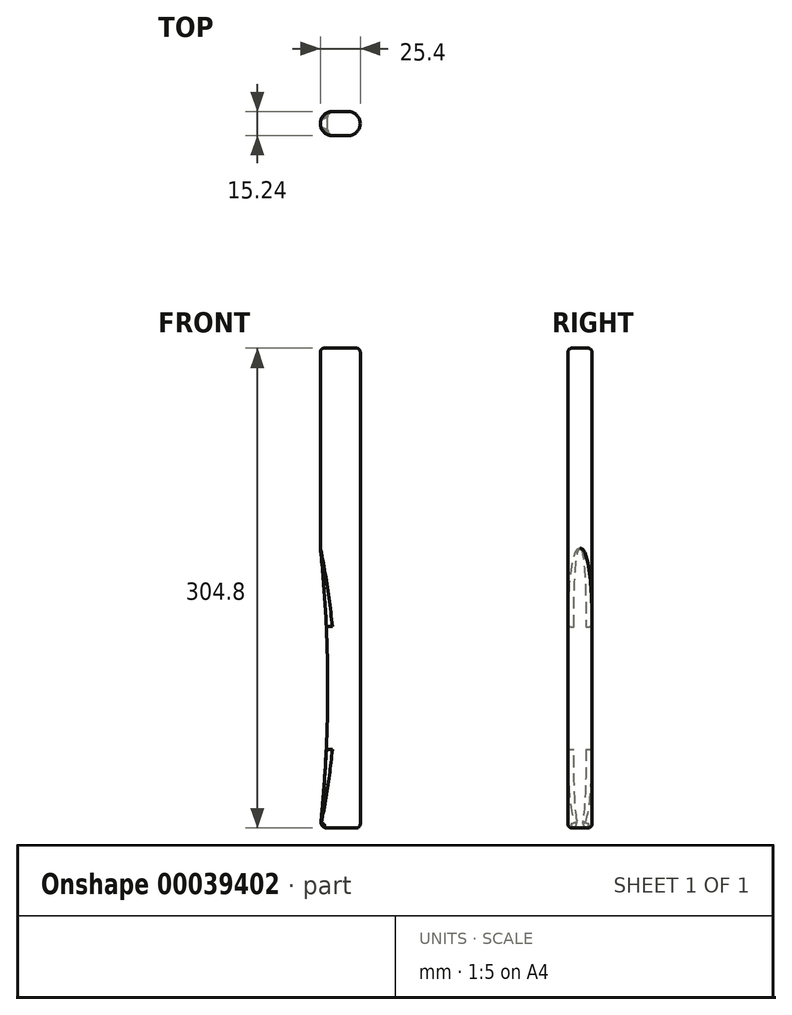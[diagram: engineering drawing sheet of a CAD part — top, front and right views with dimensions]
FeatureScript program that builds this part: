
annotation { "Feature Type Name" : "Feature", "Feature Type Description" : "" }
export const myFeature = defineFeature(function(context is Context, id is Id, definition is map)
    precondition{}
    {
        {
            var Q0;
            Q0=qCreatedBy(makeId("Front.planeOp"),FACE);
            var sketch = newSketch(context, id + "F0", { "sketchPlane" : qUnion([Q0])});
            skLineSegment(sketch, "E0", {"start": v(1.98, -144.5) * mm, "end": v(1.98, 160.3) * mm});
            skLineSegment(sketch, "E1", {"start": v(1.98, 160.3) * mm, "end": v(-23.42, 160.3) * mm});
            skLineSegment(sketch, "E2", {"start": v(-23.42, 160.3) * mm, "end": v(-23.42, 33.3) * mm});
            skLineSegment(sketch, "E3", {"start": v(1.98, -144.5) * mm, "end": v(-23.42, -144.5) * mm});
            skArc(sketch, "E4", {"start": v(-23.42, -144.5) * mm, "mid": v(-18.7, -55.6) * mm, "end": v(-23.42, 33.3) * mm});
            skSolve(sketch);
        }
        {
            var Q0;
            Q0 = qSketchRegion(id + "F0", true);
            extrude(context, id + "F1", {"entities" : qUnion([Q0]), "depth" : 15.24 * mm});
        }
        {
            var Q0;
            Q0=makeQuery(id+"F1.opExtrude","CAP_EDGE",EDGE,{"disambiguationData":[OSD([sQuery(id+"F0.wireOp",EDGE,"E0")])],"isStart":false});
            var Q1;
            Q1=makeQuery(id+"F1.opExtrude","CAP_EDGE",EDGE,{"disambiguationData":[OSD([sQuery(id+"F0.wireOp",EDGE,"E0")])],"isStart":true});
            var Q2;
            Q2=makeQuery(id+"F1.opExtrude","CAP_EDGE",EDGE,{"disambiguationData":[OSD([sQuery(id+"F0.wireOp",EDGE,"E2")])],"isStart":true});
            var Q3;
            Q3=makeQuery(id+"F1.opExtrude","CAP_EDGE",EDGE,{"disambiguationData":[OSD([sQuery(id+"F0.wireOp",EDGE,"E2")])],"isStart":false});
            var Q4;
            Q4=makeQuery(id+"F1.opExtrude","CAP_EDGE",EDGE,{"disambiguationData":[OSD([sQuery(id+"F0.wireOp",EDGE,"ed93cf97-2ccb-4e51-b4c0-a1d36dc98316")])],"isStart":true});
            var Q5;
            Q5=makeQuery(id+"F1.opExtrude","CAP_EDGE",EDGE,{"disambiguationData":[OSD([sQuery(id+"F0.wireOp",EDGE,"ed93cf97-2ccb-4e51-b4c0-a1d36dc98316")])],"isStart":false});
            fillet(context, id + "F2", {"entities" : qUnion([Q0, Q1, Q2, Q3, Q4, Q5]), "radius" : 7.62 * mm, "tangentPropagation" : true, "allowEdgeOverflow" : false});
        }
        {
            var Q0;
            Q0=makeQuery(id+"F1.opExtrude","CAP_EDGE",EDGE,{"disambiguationData":[OSD([sQuery(id+"F0.wireOp",EDGE,"E1")])],"isStart":false});
            var Q1;
            Q1=makeQuery(id+"F1.opExtrude","CAP_EDGE",EDGE,{"disambiguationData":[OSD([sQuery(id+"F0.wireOp",EDGE,"E1")])],"isStart":true});
            var Q2;
            Q2=makeQuery(id+"F2.opFillet","BLEND_EDGE",EDGE,{"blendedFrom":[makeQuery(id+"F1.opExtrude","CAP_EDGE",EDGE,{"disambiguationData":[OSD([sQuery(id+"F0.wireOp",EDGE,"E0")])],"isStart":false}),makeQuery(id+"F1.opExtrude","SWEPT_FACE",FACE,{"disambiguationData":[OSD([sQuery(id+"F0.wireOp",EDGE,"E1")])]})],"blendedInto":[makeQuery(id+"F1.opExtrude","SWEPT_FACE",FACE,{"disambiguationData":[OSD([sQuery(id+"F0.wireOp",EDGE,"E1")])]})]});
            var Q3;
            Q3=makeQuery(id+"F2.opFillet","BLEND_EDGE",EDGE,{"blendedFrom":[makeQuery(id+"F1.opExtrude","CAP_EDGE",EDGE,{"disambiguationData":[OSD([sQuery(id+"F0.wireOp",EDGE,"E2")])],"isStart":false}),makeQuery(id+"F1.opExtrude","SWEPT_FACE",FACE,{"disambiguationData":[OSD([sQuery(id+"F0.wireOp",EDGE,"E1")])]})],"blendedInto":[makeQuery(id+"F1.opExtrude","SWEPT_FACE",FACE,{"disambiguationData":[OSD([sQuery(id+"F0.wireOp",EDGE,"E1")])]})]});
            var Q4;
            Q4=makeQuery(id+"F2.opFillet","BLEND_EDGE",EDGE,{"blendedFrom":[makeQuery(id+"F1.opExtrude","CAP_EDGE",EDGE,{"disambiguationData":[OSD([sQuery(id+"F0.wireOp",EDGE,"E2")])],"isStart":false}),makeQuery(id+"F1.opExtrude","SWEPT_FACE",FACE,{"disambiguationData":[OSD([sQuery(id+"F0.wireOp",EDGE,"E3")])]})],"blendedInto":[makeQuery(id+"F1.opExtrude","SWEPT_FACE",FACE,{"disambiguationData":[OSD([sQuery(id+"F0.wireOp",EDGE,"E3")])]})]});
            fillet(context, id + "F3", {"entities" : qUnion([Q0, Q1, Q2, Q3, Q4]), "radius" : 2.54 * mm, "tangentPropagation" : true, "allowEdgeOverflow" : false});
        }
        {
            var Q0;
            Q0=makeQuery(id+"F2.opFillet","BLEND_EDGE",EDGE,{"blendedFrom":[makeQuery(id+"F1.opExtrude","CAP_EDGE",EDGE,{"disambiguationData":[OSD([sQuery(id+"F0.wireOp",EDGE,"E2")])],"isStart":false}),makeQuery(id+"F1.opExtrude","SWEPT_FACE",FACE,{"disambiguationData":[OSD([sQuery(id+"F0.wireOp",EDGE,"E4")])]})],"blendedInto":[makeQuery(id+"F1.opExtrude","SWEPT_FACE",FACE,{"disambiguationData":[OSD([sQuery(id+"F0.wireOp",EDGE,"E4")])]})]});
            var Q1;
            Q1=makeQuery(id+"F2.opFillet","BLEND_EDGE",EDGE,{"blendedFrom":[makeQuery(id+"F1.opExtrude","CAP_EDGE",EDGE,{"disambiguationData":[OSD([sQuery(id+"F0.wireOp",EDGE,"E2")])],"isStart":true}),makeQuery(id+"F1.opExtrude","SWEPT_FACE",FACE,{"disambiguationData":[OSD([sQuery(id+"F0.wireOp",EDGE,"E4")])]})],"blendedInto":[makeQuery(id+"F1.opExtrude","SWEPT_FACE",FACE,{"disambiguationData":[OSD([sQuery(id+"F0.wireOp",EDGE,"E4")])]})]});
            fillet(context, id + "F4", {"entities" : qUnion([Q0, Q1]), "radius" : 3.8 * mm, "tangentPropagation" : true, "allowEdgeOverflow" : false});
        }
    });
